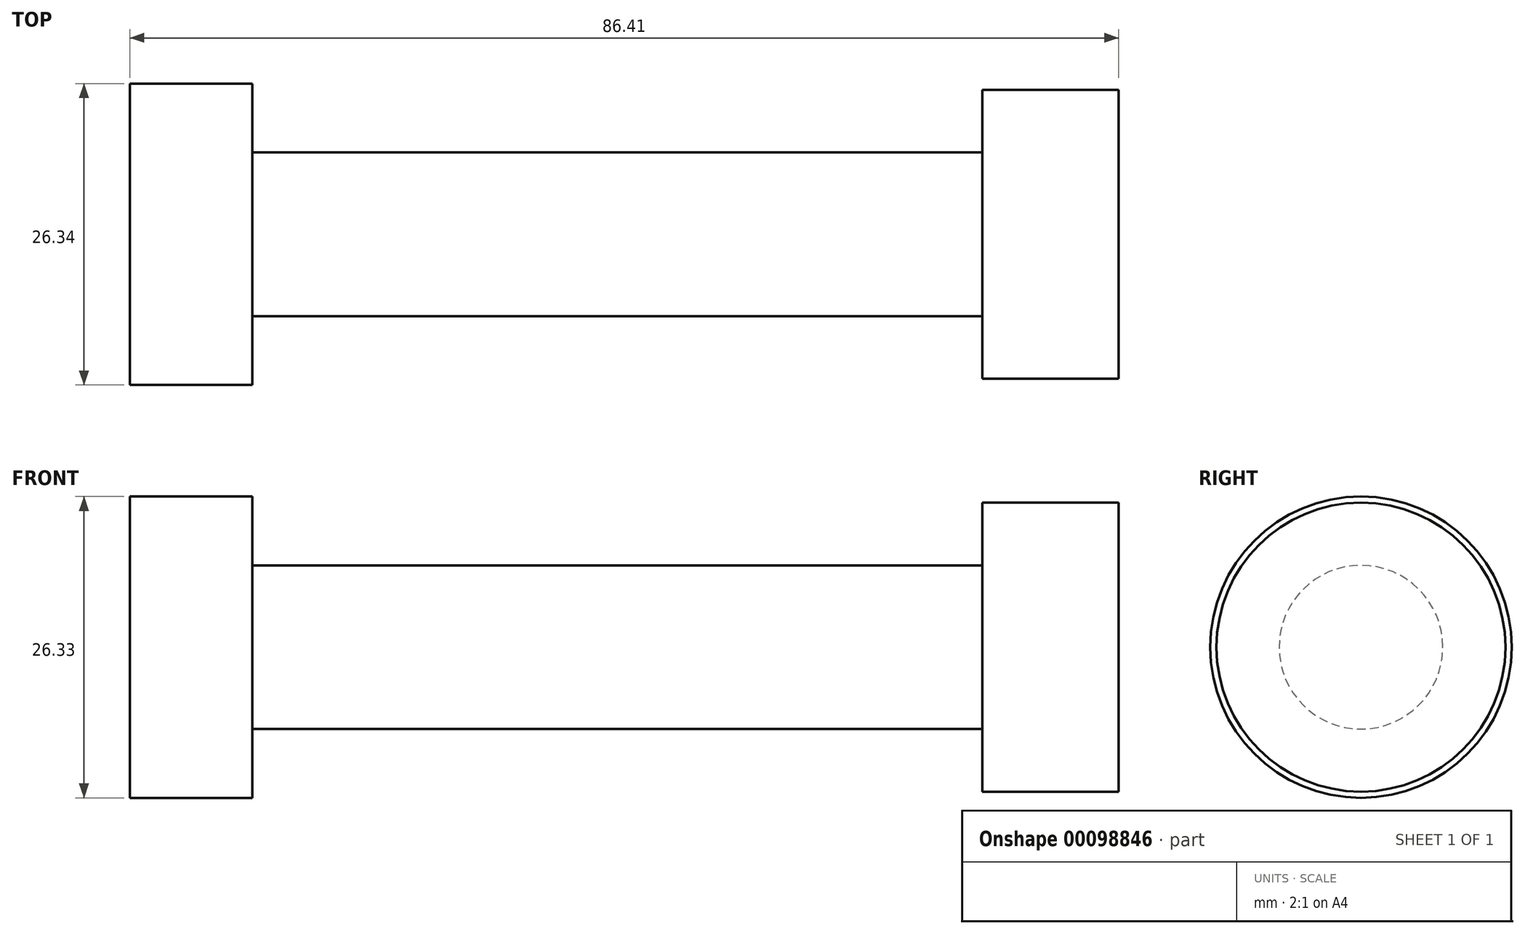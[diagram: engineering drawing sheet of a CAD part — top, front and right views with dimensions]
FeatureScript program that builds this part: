
annotation { "Feature Type Name" : "Feature", "Feature Type Description" : "" }
export const myFeature = defineFeature(function(context is Context, id is Id, definition is map)
    precondition{}
    {
        {
            var Q0;
            Q0=qCreatedBy(makeId("Front.planeOp"),FACE);
            var sketch = newSketch(context, id + "F0", { "sketchPlane" : qUnion([Q0])});
            skLineSegment(sketch, "E0", {"start": v(-47.08, 19.87) * mm, "end": v(-36.35, 19.87) * mm});
            skLineSegment(sketch, "E1", {"start": v(-36.35, 19.87) * mm, "end": v(-36.35, 13.86) * mm});
            skLineSegment(sketch, "E2", {"start": v(-36.35, 13.86) * mm, "end": v(27.41, 13.86) * mm});
            skLineSegment(sketch, "E3", {"start": v(27.41, 13.86) * mm, "end": v(27.41, 19.33) * mm});
            skLineSegment(sketch, "E4", {"start": v(27.41, 19.33) * mm, "end": v(39.33, 19.33) * mm});
            skLineSegment(sketch, "E5", {"start": v(39.33, 19.33) * mm, "end": v(39.33, 6.7) * mm});
            skLineSegment(sketch, "E6", {"start": v(39.33, 6.7) * mm, "end": v(-47.08, 6.7) * mm});
            skLineSegment(sketch, "E7", {"start": v(-47.08, 6.7) * mm, "end": v(-47.08, 19.87) * mm});
            skSolve(sketch);
        }
        {
            var Q0;
            Q0=makeQuery(id+"F0.imprint","IMPRINT",FACE,{"disambiguationData":[TD([[makeQuery(id+"F0.imprint","IMPRINT",EDGE,{"derivedFrom":sQuery(id+"F0.wireOp",EDGE,"E0")}),-1.0]])]});
            var Q1;
            Q1=sQuery(id+"F0.wireOp",EDGE,"E6");
            revolve(context, id + "F1", {"entities" : qUnion([Q0]), "axis" : qUnion([Q1]), "revolveType" : RevolveType.FULL});
        }
    });
